# Revit family: Fixture_Support_Water_Closet_Horizontal-Zurn-Z1201-H_4-FMBO
name_source: partatom
category: Plumbing Fixtures
units: mm (PartAtom-declared; Revit-internal decimal feet)

## family parameters
Always vertical = Yes
Cut with Voids When Loaded = No
Maintain Annotation Orientation = No
OmniClass Number = 23.45.55.11
OmniClass Title = Sanitary Components
Part Type = Normal
Room Calculation Point = No
Round Connector Dimension = Use Radius
Shared = No
Work Plane-Based = No

## types (2) — shared parameters
Approx. Weight (Lbs) = 44 "
Assembly Code = D2030100
CW Connection = No
Connector sketch = Yes
Coupling material = ABS - Zurn - Acrylonitrile Butadiene Styrene - Black
Default Elevation = 20 "
Description = EZCARRY® ADJUSTABLE HORIZONTAL HIGH PERFORMANCE SIPHON JET HUB AND SPIGOT WATER CLOSET CARRIER SYSTEM W/ FLOOR MOUNT BACK OUTLET FIXTURE SUPPORT
Dimension "B" = 16.25 "
Dimension "N" = 9.25 "
HW Connection = No
Hardware = Steel - Zurn - Galvanized
Horizontal pipe Axis = 6.375 "
K DIM = 4.125 "
Main Material = Iron - Zurn - Cast - Painted - Blue
Manufacturer = Zurn Water, LLC
Manufacurer Brand = Zurn
Model = Z1201-HR4-FMBO
Modified Date = 01/22/2026
Pipe Size _A Nominal Diameter = 4 "
Pipe Size _A Nominal Radius = 2 "
Pipe Size _A Outer Diameter = 4.5 "
Product Documentation Link = https://files.zurn.com
Product Installation Sheet URL = https://files.zurn.com
Product Page URL = https://www.zurn.com
Product data url = https://www.bimobject.com
Type Comments = Z1201-HR4-FMBO with 4 inch Outlet
URL = www.zurn.com
Vent Connection = Yes
Vent Connection Radius = 1 "
Vent Diameter (Actual) = 2.375 "
Vent Diameter (Nominal) = 2 "
WFU = 1
Waste Connection = Yes
Water Closet Inlet Radius = 1.5 "
Width = 13.25 "
zero-valued in all types: CWFU, HWFU

## per-type parameters (varying)
| type | Angle 2 | HL4 | HR4 | Offset Distance | Rotation angle |
| Z1201-HR4-FMBO | 270.00° | No | Yes | 4.75 " | 90.00° |
| Z1201-HL4-FMBO | 90.00° | Yes | No | 0 " | 270.00° |

## geometry (parser evidence)
native form markers: Blend x6, Sweep x3
no freeform markers — native parametric forms only
